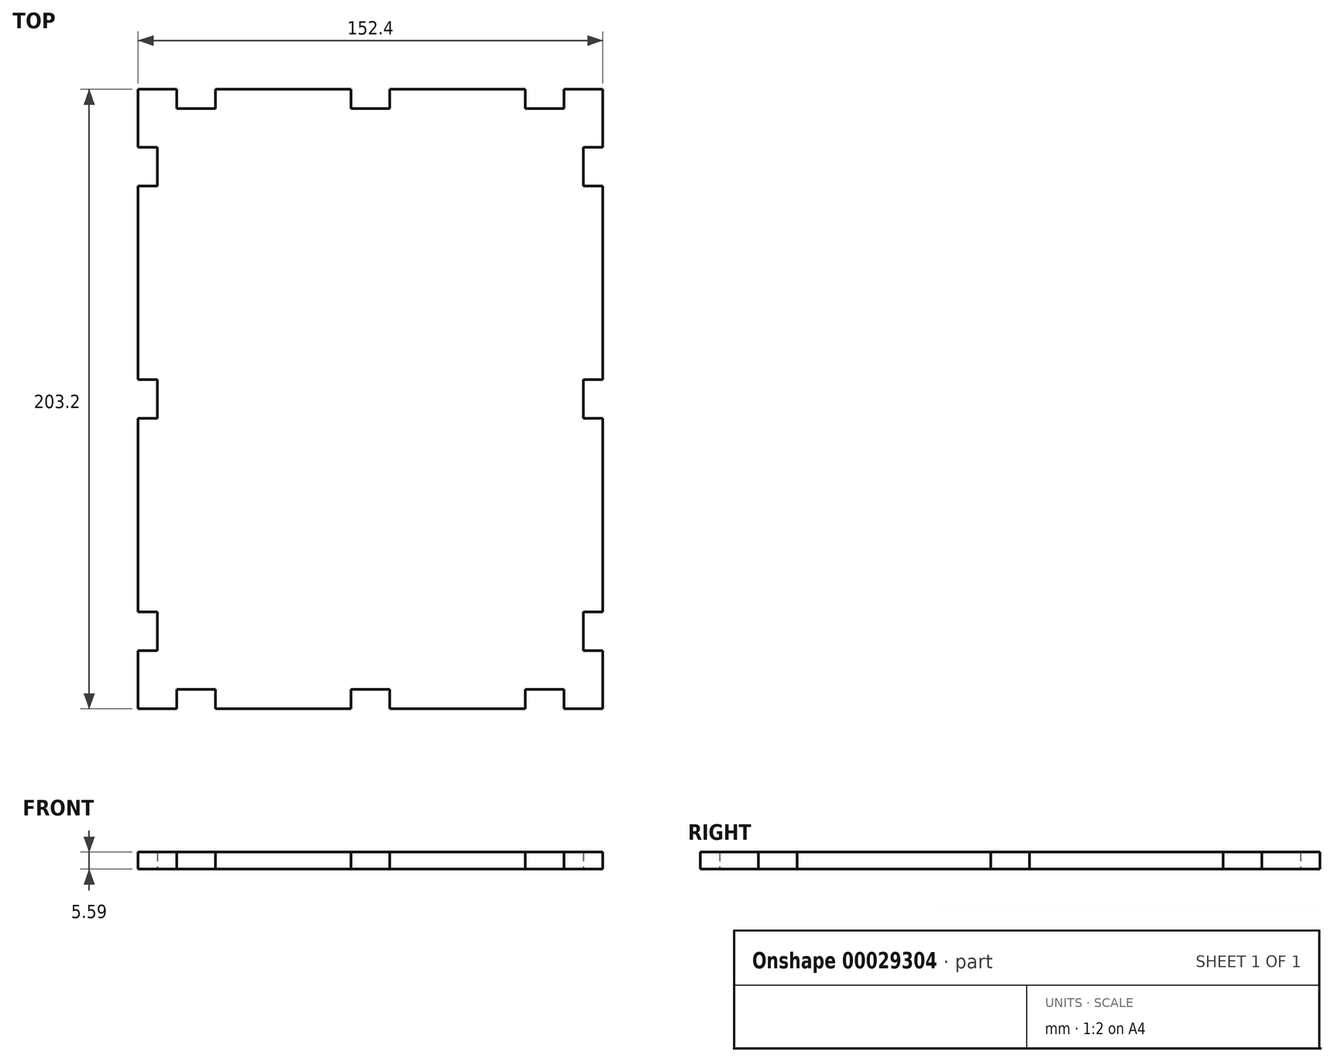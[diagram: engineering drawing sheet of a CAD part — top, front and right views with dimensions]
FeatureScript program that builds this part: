
annotation { "Feature Type Name" : "Feature", "Feature Type Description" : "" }
export const myFeature = defineFeature(function(context is Context, id is Id, definition is map)
    precondition{}
    {
        {
            var Q0;
            Q0=qCreatedBy(makeId("Top.planeOp"),FACE);
            var sketch = newSketch(context, id + "F0", { "sketchPlane" : qUnion([Q0])});
            skLineSegment(sketch, "E0", {"start": v(0, -101.6) * mm, "end": v(0, 101.6) * mm, "construction": true});
            skLineSegment(sketch, "E1", {"start": v(-76.2, 0) * mm, "end": v(76.2, 0) * mm, "construction": true});
            skLineSegment(sketch, "E2.0", {"start": v(38.1, -101.6) * mm, "end": v(38.1, 101.6) * mm, "construction": true});
            skLineSegment(sketch, "E3.0", {"start": v(76.2, -101.6) * mm, "end": v(76.2, -82.55) * mm, "construction": true});
            skLineSegment(sketch, "E4.0", {"start": v(-38.1, -101.6) * mm, "end": v(-38.1, 101.6) * mm, "construction": true});
            skLineSegment(sketch, "E5.0", {"start": v(-76.2, -101.6) * mm, "end": v(-76.2, 76.2) * mm, "construction": true});
            skLineSegment(sketch, "E6.0", {"start": v(-76.2, -50.8) * mm, "end": v(76.2, -50.8) * mm, "construction": true});
            skLineSegment(sketch, "E7.0", {"start": v(-76.2, -101.6) * mm, "end": v(-63.5, -101.6) * mm, "construction": true});
            skLineSegment(sketch, "E8.0", {"start": v(-76.2, 50.8) * mm, "end": v(76.2, 50.8) * mm, "construction": true});
            skLineSegment(sketch, "E9.0", {"start": v(-76.2, 101.6) * mm, "end": v(76.2, 101.6) * mm, "construction": true});
            skLineSegment(sketch, "E10.bottom", {"start": v(-76.2, -101.6) * mm, "end": v(-63.5, -101.6) * mm});
            skLineSegment(sketch, "E10.top", {"start": v(-76.2, 101.6) * mm, "end": v(-63.5, 101.6) * mm});
            skLineSegment(sketch, "E10.left", {"start": v(-76.2, -101.6) * mm, "end": v(-76.2, -82.55) * mm});
            skLineSegment(sketch, "E10.right", {"start": v(76.2, -101.6) * mm, "end": v(76.2, -82.55) * mm});
            skLineSegment(sketch, "E11.0", {"start": v(-57.15, -101.6) * mm, "end": v(-57.15, 101.6) * mm, "construction": true});
            skLineSegment(sketch, "E12.0", {"start": v(57.15, -101.6) * mm, "end": v(57.15, 101.6) * mm, "construction": true});
            skLineSegment(sketch, "E13.0", {"start": v(-76.2, -76.2) * mm, "end": v(76.2, -76.2) * mm, "construction": true});
            skLineSegment(sketch, "E14.0", {"start": v(-76.2, 76.2) * mm, "end": v(76.2, 76.2) * mm, "construction": true});
            skLineSegment(sketch, "E15.0", {"start": v(-76.2, -69.85) * mm, "end": v(76.2, -69.85) * mm, "construction": true});
            skLineSegment(sketch, "E16.0", {"start": v(-76.2, -82.55) * mm, "end": v(76.2, -82.55) * mm, "construction": true});
            skLineSegment(sketch, "E17.0", {"start": v(-69.85, -101.6) * mm, "end": v(-69.85, 101.6) * mm, "construction": true});
            skLineSegment(sketch, "E18.0", {"start": v(-76.2, -95.25) * mm, "end": v(76.2, -95.25) * mm, "construction": true});
            skLineSegment(sketch, "E19.0", {"start": v(-76.2, 95.25) * mm, "end": v(76.2, 95.25) * mm, "construction": true});
            skLineSegment(sketch, "E20.0", {"start": v(69.85, -101.6) * mm, "end": v(69.85, 101.6) * mm, "construction": true});
            skLineSegment(sketch, "E21", {"start": v(-76.2, -82.55) * mm, "end": v(-69.85, -82.55) * mm});
            skLineSegment(sketch, "E22", {"start": v(-69.85, -82.55) * mm, "end": v(-69.85, -69.85) * mm});
            skLineSegment(sketch, "E23", {"start": v(-69.85, -69.85) * mm, "end": v(-76.2, -69.85) * mm});
            skLineSegment(sketch, "E24", {"start": v(76.2, -82.55) * mm, "end": v(69.85, -82.55) * mm});
            skLineSegment(sketch, "E25", {"start": v(69.85, -82.55) * mm, "end": v(69.85, -69.85) * mm});
            skLineSegment(sketch, "E26", {"start": v(69.85, -69.85) * mm, "end": v(76.2, -69.85) * mm});
            skLineSegment(sketch, "E27.0", {"start": v(-76.2, 6.35) * mm, "end": v(76.2, 6.35) * mm, "construction": true});
            skLineSegment(sketch, "E28.0", {"start": v(-76.2, -6.35) * mm, "end": v(76.2, -6.35) * mm, "construction": true});
            skLineSegment(sketch, "E29", {"start": v(-76.2, -6.35) * mm, "end": v(-69.85, -6.35) * mm});
            skLineSegment(sketch, "E30.0", {"start": v(-76.2, 82.55) * mm, "end": v(76.2, 82.55) * mm, "construction": true});
            skLineSegment(sketch, "E31.0", {"start": v(-76.2, 69.85) * mm, "end": v(76.2, 69.85) * mm, "construction": true});
            skLineSegment(sketch, "E32", {"start": v(-69.85, -6.35) * mm, "end": v(-69.85, 6.35) * mm});
            skLineSegment(sketch, "E33", {"start": v(-69.85, 6.35) * mm, "end": v(-76.2, 6.35) * mm});
            skLineSegment(sketch, "E34", {"start": v(-76.2, 69.85) * mm, "end": v(-69.85, 69.85) * mm});
            skLineSegment(sketch, "E35", {"start": v(-69.85, 69.85) * mm, "end": v(-69.85, 82.55) * mm});
            skLineSegment(sketch, "E36", {"start": v(-69.85, 82.55) * mm, "end": v(-76.2, 82.55) * mm});
            skLineSegment(sketch, "E37", {"start": v(76.2, 69.85) * mm, "end": v(69.85, 69.85) * mm});
            skLineSegment(sketch, "E38", {"start": v(69.85, 69.85) * mm, "end": v(69.85, 82.55) * mm});
            skLineSegment(sketch, "E39", {"start": v(69.85, 82.55) * mm, "end": v(76.2, 82.55) * mm});
            skLineSegment(sketch, "E40", {"start": v(76.2, 6.35) * mm, "end": v(69.85, 6.35) * mm});
            skLineSegment(sketch, "E41", {"start": v(69.85, 6.35) * mm, "end": v(69.85, -6.35) * mm});
            skLineSegment(sketch, "E42", {"start": v(69.85, -6.35) * mm, "end": v(76.2, -6.35) * mm});
            skLineSegment(sketch, "E43.0", {"start": v(-63.5, -101.6) * mm, "end": v(-63.5, 101.6) * mm, "construction": true});
            skLineSegment(sketch, "E44.0", {"start": v(-50.8, -101.6) * mm, "end": v(-50.8, 101.6) * mm, "construction": true});
            skLineSegment(sketch, "E45.0", {"start": v(-6.35, -101.6) * mm, "end": v(-6.35, 101.6) * mm, "construction": true});
            skLineSegment(sketch, "E46.0", {"start": v(6.35, -101.6) * mm, "end": v(6.35, 101.6) * mm, "construction": true});
            skLineSegment(sketch, "E47.0", {"start": v(50.8, -101.6) * mm, "end": v(50.8, 101.6) * mm, "construction": true});
            skLineSegment(sketch, "E48.0", {"start": v(63.5, -101.6) * mm, "end": v(63.5, 101.6) * mm, "construction": true});
            skLineSegment(sketch, "E49", {"start": v(-63.5, -101.6) * mm, "end": v(-63.5, -95.25) * mm});
            skLineSegment(sketch, "E50", {"start": v(-63.5, -95.25) * mm, "end": v(-50.8, -95.25) * mm});
            skLineSegment(sketch, "E51", {"start": v(-50.8, -95.25) * mm, "end": v(-50.8, -101.6) * mm});
            skLineSegment(sketch, "E52", {"start": v(-6.35, -101.6) * mm, "end": v(-6.35, -95.25) * mm});
            skLineSegment(sketch, "E53", {"start": v(-6.35, -95.25) * mm, "end": v(6.35, -95.25) * mm});
            skLineSegment(sketch, "E54", {"start": v(6.35, -95.25) * mm, "end": v(6.35, -101.6) * mm});
            skLineSegment(sketch, "E55", {"start": v(50.8, -101.6) * mm, "end": v(50.8, -95.25) * mm});
            skLineSegment(sketch, "E56", {"start": v(50.8, -95.25) * mm, "end": v(63.5, -95.25) * mm});
            skLineSegment(sketch, "E57", {"start": v(63.5, -95.25) * mm, "end": v(63.5, -101.6) * mm});
            skLineSegment(sketch, "E58.trimOffspring", {"start": v(63.5, -101.6) * mm, "end": v(76.2, -101.6) * mm});
            skLineSegment(sketch, "E59.trimOffspring", {"start": v(76.2, -69.85) * mm, "end": v(76.2, -6.35) * mm});
            skLineSegment(sketch, "E60.trimOffspring", {"start": v(76.2, -69.85) * mm, "end": v(76.2, -6.35) * mm, "construction": true});
            skLineSegment(sketch, "E61.trimOffspring", {"start": v(76.2, 6.35) * mm, "end": v(76.2, 69.85) * mm});
            skLineSegment(sketch, "E62.trimOffspring", {"start": v(76.2, 6.35) * mm, "end": v(76.2, 69.85) * mm, "construction": true});
            skLineSegment(sketch, "E63.trimOffspring", {"start": v(76.2, 82.55) * mm, "end": v(76.2, 101.6) * mm});
            skLineSegment(sketch, "E64.trimOffspring", {"start": v(76.2, 82.55) * mm, "end": v(76.2, 101.6) * mm, "construction": true});
            skLineSegment(sketch, "E65.trimOffspring", {"start": v(-76.2, 82.55) * mm, "end": v(-76.2, 101.6) * mm});
            skLineSegment(sketch, "E66.trimOffspring", {"start": v(-76.2, 82.55) * mm, "end": v(-76.2, 101.6) * mm, "construction": true});
            skLineSegment(sketch, "E67.trimOffspring", {"start": v(-76.2, 6.35) * mm, "end": v(-76.2, 69.85) * mm});
            skLineSegment(sketch, "E68.trimOffspring", {"start": v(-76.2, -69.85) * mm, "end": v(-76.2, -6.35) * mm});
            skLineSegment(sketch, "E69.trimOffspring", {"start": v(-50.8, -101.6) * mm, "end": v(-6.35, -101.6) * mm});
            skLineSegment(sketch, "E70.trimOffspring", {"start": v(-57.15, -101.6) * mm, "end": v(76.2, -101.6) * mm, "construction": true});
            skLineSegment(sketch, "E71.trimOffspring", {"start": v(6.35, -101.6) * mm, "end": v(50.8, -101.6) * mm});
            skLineSegment(sketch, "E72", {"start": v(-63.5, 101.6) * mm, "end": v(-63.5, 95.25) * mm});
            skLineSegment(sketch, "E73", {"start": v(-63.5, 95.25) * mm, "end": v(-50.8, 95.25) * mm});
            skLineSegment(sketch, "E74", {"start": v(-50.8, 95.25) * mm, "end": v(-50.8, 101.6) * mm});
            skLineSegment(sketch, "E75", {"start": v(-6.35, 101.6) * mm, "end": v(-6.35, 95.25) * mm});
            skLineSegment(sketch, "E76", {"start": v(-6.35, 95.25) * mm, "end": v(6.35, 95.25) * mm});
            skLineSegment(sketch, "E77", {"start": v(6.35, 95.25) * mm, "end": v(6.35, 101.6) * mm});
            skLineSegment(sketch, "E78", {"start": v(50.8, 101.6) * mm, "end": v(50.8, 95.25) * mm});
            skLineSegment(sketch, "E79", {"start": v(50.8, 95.25) * mm, "end": v(63.5, 95.25) * mm});
            skLineSegment(sketch, "E80", {"start": v(63.5, 95.25) * mm, "end": v(63.5, 101.6) * mm});
            skLineSegment(sketch, "E81.trimOffspring", {"start": v(63.5, 101.6) * mm, "end": v(76.2, 101.6) * mm});
            skLineSegment(sketch, "E82.trimOffspring", {"start": v(6.35, 101.6) * mm, "end": v(50.8, 101.6) * mm});
            skLineSegment(sketch, "E83.trimOffspring", {"start": v(-50.8, 101.6) * mm, "end": v(-6.35, 101.6) * mm});
            skSolve(sketch);
        }
        {
            var Q0;
            Q0=makeQuery(id+"F0.imprint","IMPRINT",FACE,{"disambiguationData":[TD([[makeQuery(id+"F0.imprint","IMPRINT",EDGE,{"derivedFrom":sQuery(id+"F0.wireOp",EDGE,"E10.bottom")}),1.0]])]});
            extrude(context, id + "F1", {"entities" : qUnion([Q0]), "depth" : 5.6 * mm});
        }
    });
